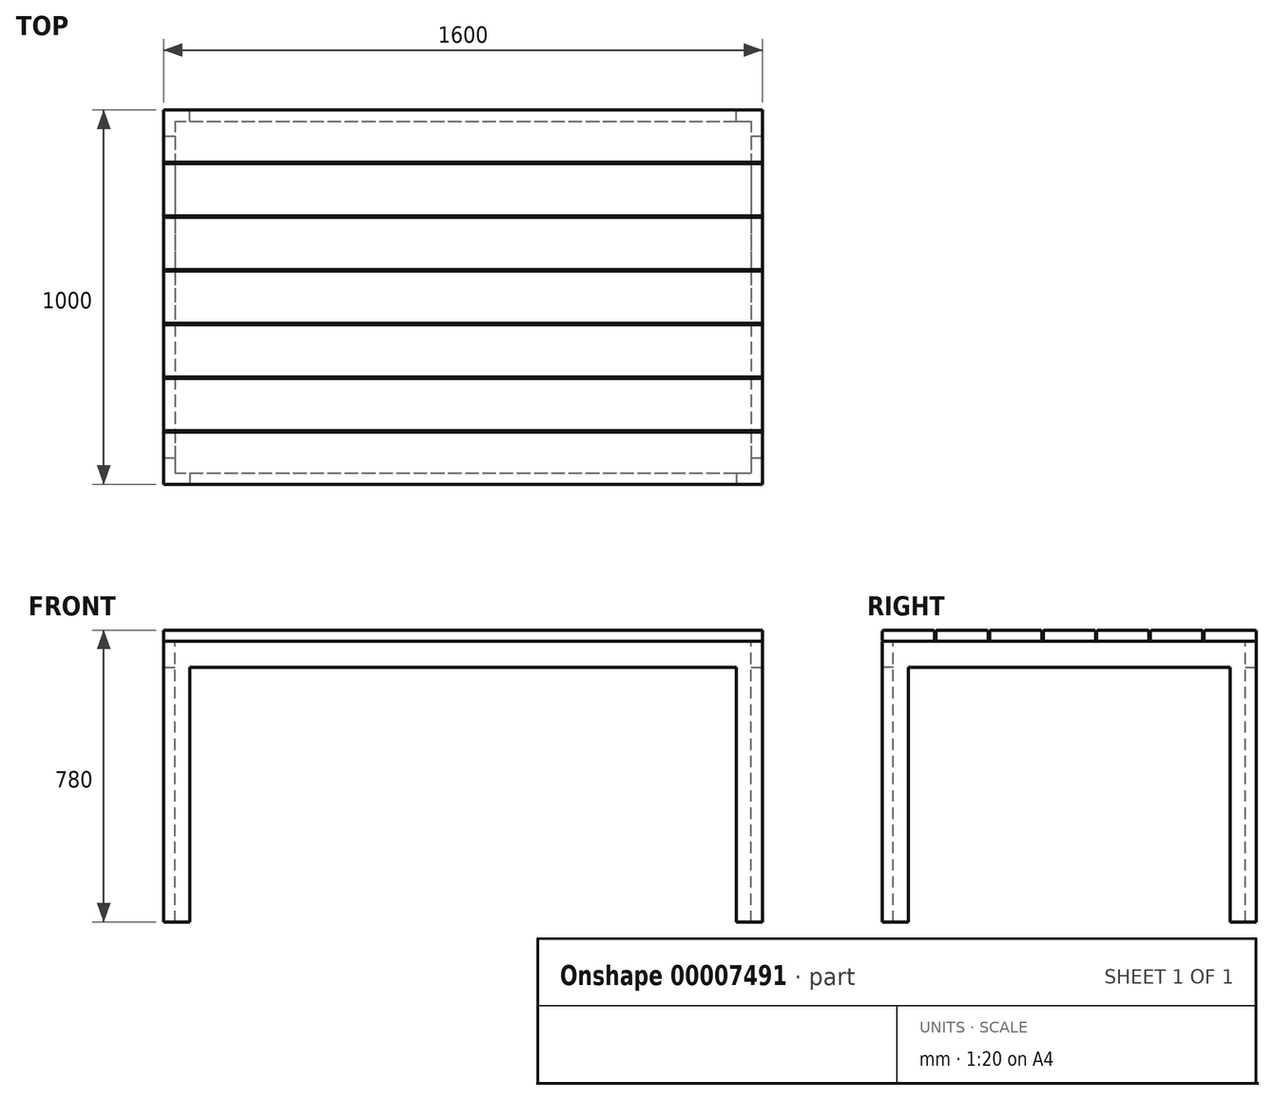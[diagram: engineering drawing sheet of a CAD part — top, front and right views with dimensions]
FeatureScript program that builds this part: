
annotation { "Feature Type Name" : "Feature", "Feature Type Description" : "" }
export const myFeature = defineFeature(function(context is Context, id is Id, definition is map)
    precondition{}
    {
        {
            var Q0;
            Q0=qCreatedBy(makeId("Top.planeOp"),FACE);
            var sketch = newSketch(context, id + "F0", { "sketchPlane" : qUnion([Q0])});
            skLineSegment(sketch, "E0.rect.bottom", {"start": v(-800, 500) * mm, "end": v(800, 500) * mm});
            skLineSegment(sketch, "E0.rect.top", {"start": v(-800, -500) * mm, "end": v(800, -500) * mm});
            skLineSegment(sketch, "E0.rect.left", {"start": v(-800, 500) * mm, "end": v(-800, -500) * mm});
            skLineSegment(sketch, "E0.rect.right", {"start": v(800, 500) * mm, "end": v(800, -500) * mm});
            skPoint(sketch, "E0.rect.middle", {"position": v(0, 0) * mm});
            skLineSegment(sketch, "E1.rect.bottom", {"start": v(-770, 470) * mm, "end": v(770, 470) * mm});
            skLineSegment(sketch, "E1.rect.top", {"start": v(-770, -470) * mm, "end": v(770, -470) * mm});
            skLineSegment(sketch, "E1.rect.left", {"start": v(-770, 470) * mm, "end": v(-770, -470) * mm});
            skLineSegment(sketch, "E1.rect.right", {"start": v(770, 470) * mm, "end": v(770, -470) * mm});
            skLineSegment(sketch, "E2", {"start": v(-800, -430) * mm, "end": v(-770, -430) * mm});
            skLineSegment(sketch, "E3", {"start": v(-730, -470) * mm, "end": v(-730, -500) * mm});
            skLineSegment(sketch, "E4", {"start": v(-800, 430) * mm, "end": v(-770, 430) * mm});
            skLineSegment(sketch, "E5", {"start": v(-730, 470) * mm, "end": v(-730, 500) * mm});
            skLineSegment(sketch, "E6", {"start": v(730, 470) * mm, "end": v(730, 500) * mm});
            skLineSegment(sketch, "E7", {"start": v(770, 430) * mm, "end": v(800, 430) * mm});
            skLineSegment(sketch, "E8", {"start": v(770, -430) * mm, "end": v(800, -430) * mm});
            skLineSegment(sketch, "E9", {"start": v(730, -470) * mm, "end": v(730, -500) * mm});
            skSolve(sketch);
        }
        {
            var Q0;
            {var subQ1=sQuery(id+"F0.wireOp",EDGE,"E2");Q0=makeQuery(id+"F0.imprint","IMPRINT",FACE,{"disambiguationData":[TD([[makeQuery(id+"F0.imprint","IMPRINT",EDGE,{"derivedFrom":subQ1}),-1.0]])]});}
            var Q1;
            {var subQ0=sQuery(id+"F0.wireOp",EDGE,"E4");Q1=makeQuery(id+"F0.imprint","IMPRINT",FACE,{"disambiguationData":[TD([[makeQuery(id+"F0.imprint","IMPRINT",EDGE,{"derivedFrom":subQ0}),1.0]])]});}
            var Q2;
            {var subQ1=sQuery(id+"F0.wireOp",EDGE,"E6");Q2=makeQuery(id+"F0.imprint","IMPRINT",FACE,{"disambiguationData":[TD([[makeQuery(id+"F0.imprint","IMPRINT",EDGE,{"derivedFrom":subQ1}),-1.0]])]});}
            var Q3;
            {var subQ1=sQuery(id+"F0.wireOp",EDGE,"E8");Q3=makeQuery(id+"F0.imprint","IMPRINT",FACE,{"disambiguationData":[TD([[makeQuery(id+"F0.imprint","IMPRINT",EDGE,{"derivedFrom":subQ1}),-1.0]])]});}
            extrude(context, id + "F1", {"entities" : qUnion([Q0, Q1, Q2, Q3]), "oppositeDirection" : true, "depth" : 750 * mm});
        }
        {
            var Q0;
            {var subQ1=sQuery(id+"F0.wireOp",EDGE,"E2");Q0=makeQuery(id+"F0.imprint","IMPRINT",FACE,{"disambiguationData":[TD([[makeQuery(id+"F0.imprint","IMPRINT",EDGE,{"derivedFrom":subQ1}),1.0]])]});}
            var Q1;
            {var subQ1=sQuery(id+"F0.wireOp",EDGE,"E5");Q1=makeQuery(id+"F0.imprint","IMPRINT",FACE,{"disambiguationData":[TD([[makeQuery(id+"F0.imprint","IMPRINT",EDGE,{"derivedFrom":subQ1}),-1.0]])]});}
            var Q2;
            {var subQ1=sQuery(id+"F0.wireOp",EDGE,"E3");Q2=makeQuery(id+"F0.imprint","IMPRINT",FACE,{"disambiguationData":[TD([[makeQuery(id+"F0.imprint","IMPRINT",EDGE,{"derivedFrom":subQ1}),1.0]])]});}
            var Q3;
            {var subQ1=sQuery(id+"F0.wireOp",EDGE,"E7");Q3=makeQuery(id+"F0.imprint","IMPRINT",FACE,{"disambiguationData":[TD([[makeQuery(id+"F0.imprint","IMPRINT",EDGE,{"derivedFrom":subQ1}),-1.0]])]});}
            extrude(context, id + "F2", {"entities" : qUnion([Q0, Q1, Q2, Q3]), "operationType" : NewBodyOperationType.ADD, "oppositeDirection" : true, "depth" : 70 * mm});
        }
        {
            var Q0;
            Q0=qCreatedBy(makeId("Top.planeOp"),FACE);
            var sketch = newSketch(context, id + "F3", { "sketchPlane" : qUnion([Q0])});
            skLineSegment(sketch, "E10.bottom", {"start": v(-800, -500) * mm, "end": v(800, -500) * mm});
            skLineSegment(sketch, "E10.top", {"start": v(-800, -360.3) * mm, "end": v(800, -360.3) * mm});
            skLineSegment(sketch, "E10.left", {"start": v(-800, -500) * mm, "end": v(-800, -360.3) * mm});
            skLineSegment(sketch, "E10.right", {"start": v(800, -500) * mm, "end": v(800, -360.3) * mm});
            skLineSegment(sketch, "E11.0.1.0", {"start": v(-800, -356.62) * mm, "end": v(-800, -216.92) * mm});
            skLineSegment(sketch, "E11.0.1.1", {"start": v(-800, -356.62) * mm, "end": v(800, -356.62) * mm});
            skLineSegment(sketch, "E11.0.1.2", {"start": v(-800, -216.92) * mm, "end": v(800, -216.92) * mm});
            skLineSegment(sketch, "E11.0.1.3", {"start": v(800, -356.62) * mm, "end": v(800, -216.92) * mm});
            skLineSegment(sketch, "E11.0.2.0", {"start": v(-800, -213.23) * mm, "end": v(-800, -73.53) * mm});
            skLineSegment(sketch, "E11.0.2.1", {"start": v(-800, -213.23) * mm, "end": v(800, -213.23) * mm});
            skLineSegment(sketch, "E11.0.2.2", {"start": v(-800, -73.53) * mm, "end": v(800, -73.53) * mm});
            skLineSegment(sketch, "E11.0.2.3", {"start": v(800, -213.23) * mm, "end": v(800, -73.53) * mm});
            skLineSegment(sketch, "E11.0.3.0", {"start": v(-800, -69.85) * mm, "end": v(-800, 69.85) * mm});
            skLineSegment(sketch, "E11.0.3.1", {"start": v(-800, -69.85) * mm, "end": v(800, -69.85) * mm});
            skLineSegment(sketch, "E11.0.3.2", {"start": v(-800, 69.85) * mm, "end": v(800, 69.85) * mm});
            skLineSegment(sketch, "E11.0.3.3", {"start": v(800, -69.85) * mm, "end": v(800, 69.85) * mm});
            skLineSegment(sketch, "E11.0.4.0", {"start": v(-800, 73.53) * mm, "end": v(-800, 213.23) * mm});
            skLineSegment(sketch, "E11.0.4.1", {"start": v(-800, 73.53) * mm, "end": v(800, 73.53) * mm});
            skLineSegment(sketch, "E11.0.4.2", {"start": v(-800, 213.23) * mm, "end": v(800, 213.23) * mm});
            skLineSegment(sketch, "E11.0.4.3", {"start": v(800, 73.53) * mm, "end": v(800, 213.23) * mm});
            skLineSegment(sketch, "E11.0.5.0", {"start": v(-800, 216.92) * mm, "end": v(-800, 356.62) * mm});
            skLineSegment(sketch, "E11.0.5.1", {"start": v(-800, 216.92) * mm, "end": v(800, 216.92) * mm});
            skLineSegment(sketch, "E11.0.5.2", {"start": v(-800, 356.62) * mm, "end": v(800, 356.62) * mm});
            skLineSegment(sketch, "E11.0.5.3", {"start": v(800, 216.92) * mm, "end": v(800, 356.62) * mm});
            skLineSegment(sketch, "E11.0.6.0", {"start": v(-800, 360.3) * mm, "end": v(-800, 500) * mm});
            skLineSegment(sketch, "E11.0.6.1", {"start": v(-800, 360.3) * mm, "end": v(800, 360.3) * mm});
            skLineSegment(sketch, "E11.0.6.2", {"start": v(-800, 500) * mm, "end": v(800, 500) * mm});
            skLineSegment(sketch, "E11.0.6.3", {"start": v(800, 360.3) * mm, "end": v(800, 500) * mm});
            skLineSegment(sketch, "E11.direction1", {"start": v(-800, -500) * mm, "end": v(-774.6, -500) * mm, "construction": true});
            skLineSegment(sketch, "E11.direction2", {"start": v(-800, -500) * mm, "end": v(-800, -356.62) * mm, "construction": true});
            skSolve(sketch);
        }
        {
            var Q0;
            Q0=makeQuery(id+"F3.imprint","IMPRINT",FACE,{"disambiguationData":[TD([[makeQuery(id+"F3.imprint","IMPRINT",EDGE,{"derivedFrom":sQuery(id+"F3.wireOp",EDGE,"E10.bottom")}),1.0]])]});
            var Q1;
            Q1=makeQuery(id+"F3.imprint","IMPRINT",FACE,{"disambiguationData":[TD([[makeQuery(id+"F3.imprint","IMPRINT",EDGE,{"derivedFrom":sQuery(id+"F3.wireOp",EDGE,"E11.0.1.0")}),-1.0]])]});
            var Q2;
            Q2=makeQuery(id+"F3.imprint","IMPRINT",FACE,{"disambiguationData":[TD([[makeQuery(id+"F3.imprint","IMPRINT",EDGE,{"derivedFrom":sQuery(id+"F3.wireOp",EDGE,"E11.0.2.0")}),-1.0]])]});
            var Q3;
            Q3=makeQuery(id+"F3.imprint","IMPRINT",FACE,{"disambiguationData":[TD([[makeQuery(id+"F3.imprint","IMPRINT",EDGE,{"derivedFrom":sQuery(id+"F3.wireOp",EDGE,"E11.0.3.0")}),-1.0]])]});
            var Q4;
            Q4=makeQuery(id+"F3.imprint","IMPRINT",FACE,{"disambiguationData":[TD([[makeQuery(id+"F3.imprint","IMPRINT",EDGE,{"derivedFrom":sQuery(id+"F3.wireOp",EDGE,"E11.0.4.0")}),-1.0]])]});
            var Q5;
            Q5=makeQuery(id+"F3.imprint","IMPRINT",FACE,{"disambiguationData":[TD([[makeQuery(id+"F3.imprint","IMPRINT",EDGE,{"derivedFrom":sQuery(id+"F3.wireOp",EDGE,"E11.0.5.0")}),-1.0]])]});
            var Q6;
            Q6=makeQuery(id+"F3.imprint","IMPRINT",FACE,{"disambiguationData":[TD([[makeQuery(id+"F3.imprint","IMPRINT",EDGE,{"derivedFrom":sQuery(id+"F3.wireOp",EDGE,"E11.0.6.0")}),-1.0]])]});
            var Q7;
            Q7=makeQuery(id+"F3.imprint","IMPRINT",FACE,{"disambiguationData":[TD([[makeQuery(id+"F3.imprint","IMPRINT",EDGE,{"derivedFrom":sQuery(id+"F3.wireOp",EDGE,"E11.0.7.0")}),-1.0]])]});
            var Q8;
            Q8=makeQuery(id+"F3.imprint","IMPRINT",FACE,{"disambiguationData":[TD([[makeQuery(id+"F3.imprint","IMPRINT",EDGE,{"derivedFrom":sQuery(id+"F3.wireOp",EDGE,"E11.0.8.0")}),-1.0]])]});
            var Q9;
            Q9=makeQuery(id+"F3.imprint","IMPRINT",FACE,{"disambiguationData":[TD([[makeQuery(id+"F3.imprint","IMPRINT",EDGE,{"derivedFrom":sQuery(id+"F3.wireOp",EDGE,"E11.0.9.0")}),-1.0]])]});
            var Q10;
            Q10=makeQuery(id+"F3.imprint","IMPRINT",FACE,{"disambiguationData":[TD([[makeQuery(id+"F3.imprint","IMPRINT",EDGE,{"derivedFrom":sQuery(id+"F3.wireOp",EDGE,"E11.0.10.0")}),-1.0]])]});
            extrude(context, id + "F4", {"entities" : qUnion([Q0, Q1, Q2, Q3, Q4, Q5, Q6, Q7, Q8, Q9, Q10]), "depth" : 30 * mm});
        }
        {
            var Q0;
            Q0=makeQuery(id+"F4.opExtrude","CAP_EDGE",EDGE,{"disambiguationData":[OSD([sQuery(id+"F3.wireOp",EDGE,"E11.0.8.1")])],"isStart":false});
            var Q1;
            Q1=makeQuery(id+"F4.opExtrude","CAP_EDGE",EDGE,{"disambiguationData":[OSD([sQuery(id+"F3.wireOp",EDGE,"E11.0.10.1")])],"isStart":false});
            var Q2;
            Q2=makeQuery(id+"F4.opExtrude","CAP_EDGE",EDGE,{"disambiguationData":[OSD([sQuery(id+"F3.wireOp",EDGE,"E10.bottom")])],"isStart":false});
            var Q3;
            Q3=makeQuery(id+"F4.opExtrude","CAP_EDGE",EDGE,{"disambiguationData":[OSD([sQuery(id+"F3.wireOp",EDGE,"E11.0.2.1")])],"isStart":false});
            var Q4;
            Q4=makeQuery(id+"F4.opExtrude","CAP_EDGE",EDGE,{"disambiguationData":[OSD([sQuery(id+"F3.wireOp",EDGE,"E10.top")])],"isStart":false});
            var Q5;
            Q5=makeQuery(id+"F4.opExtrude","CAP_EDGE",EDGE,{"disambiguationData":[OSD([sQuery(id+"F3.wireOp",EDGE,"E11.0.6.1")])],"isStart":false});
            var Q6;
            Q6=makeQuery(id+"F4.opExtrude","CAP_EDGE",EDGE,{"disambiguationData":[OSD([sQuery(id+"F3.wireOp",EDGE,"E11.0.4.1")])],"isStart":false});
            var Q7;
            Q7=makeQuery(id+"F4.opExtrude","CAP_EDGE",EDGE,{"disambiguationData":[OSD([sQuery(id+"F3.wireOp",EDGE,"E11.0.2.2")])],"isStart":false});
            var Q8;
            Q8=makeQuery(id+"F4.opExtrude","CAP_EDGE",EDGE,{"disambiguationData":[OSD([sQuery(id+"F3.wireOp",EDGE,"E11.0.10.2")])],"isStart":false});
            var Q9;
            Q9=makeQuery(id+"F4.opExtrude","CAP_EDGE",EDGE,{"disambiguationData":[OSD([sQuery(id+"F3.wireOp",EDGE,"E11.0.8.2")])],"isStart":false});
            var Q10;
            Q10=makeQuery(id+"F4.opExtrude","CAP_EDGE",EDGE,{"disambiguationData":[OSD([sQuery(id+"F3.wireOp",EDGE,"E11.0.6.2")])],"isStart":false});
            var Q11;
            Q11=makeQuery(id+"F4.opExtrude","CAP_EDGE",EDGE,{"disambiguationData":[OSD([sQuery(id+"F3.wireOp",EDGE,"E11.0.4.2")])],"isStart":false});
            var Q12;
            Q12=makeQuery(id+"F4.opExtrude","CAP_EDGE",EDGE,{"disambiguationData":[OSD([sQuery(id+"F3.wireOp",EDGE,"E11.0.9.1")])],"isStart":false});
            var Q13;
            Q13=makeQuery(id+"F4.opExtrude","CAP_EDGE",EDGE,{"disambiguationData":[OSD([sQuery(id+"F3.wireOp",EDGE,"E11.0.7.1")])],"isStart":false});
            var Q14;
            Q14=makeQuery(id+"F4.opExtrude","CAP_EDGE",EDGE,{"disambiguationData":[OSD([sQuery(id+"F3.wireOp",EDGE,"E11.0.5.1")])],"isStart":false});
            var Q15;
            Q15=makeQuery(id+"F4.opExtrude","CAP_EDGE",EDGE,{"disambiguationData":[OSD([sQuery(id+"F3.wireOp",EDGE,"E11.0.3.1")])],"isStart":false});
            var Q16;
            Q16=makeQuery(id+"F4.opExtrude","CAP_EDGE",EDGE,{"disambiguationData":[OSD([sQuery(id+"F3.wireOp",EDGE,"E11.0.3.2")])],"isStart":false});
            var Q17;
            Q17=makeQuery(id+"F4.opExtrude","CAP_EDGE",EDGE,{"disambiguationData":[OSD([sQuery(id+"F3.wireOp",EDGE,"E11.0.1.2")])],"isStart":false});
            var Q18;
            Q18=makeQuery(id+"F4.opExtrude","CAP_EDGE",EDGE,{"disambiguationData":[OSD([sQuery(id+"F3.wireOp",EDGE,"E11.0.7.2")])],"isStart":false});
            var Q19;
            Q19=makeQuery(id+"F4.opExtrude","CAP_EDGE",EDGE,{"disambiguationData":[OSD([sQuery(id+"F3.wireOp",EDGE,"E11.0.9.2")])],"isStart":false});
            var Q20;
            Q20=makeQuery(id+"F4.opExtrude","CAP_EDGE",EDGE,{"disambiguationData":[OSD([sQuery(id+"F3.wireOp",EDGE,"E11.0.5.2")])],"isStart":false});
            var Q21;
            Q21=makeQuery(id+"F4.opExtrude","CAP_EDGE",EDGE,{"disambiguationData":[OSD([sQuery(id+"F3.wireOp",EDGE,"E11.0.1.1")])],"isStart":false});
            var Q22;
            Q22=makeQuery(id+"F4.opExtrude","CAP_EDGE",EDGE,{"disambiguationData":[OSD([sQuery(id+"F3.wireOp",EDGE,"E10.bottom")])],"isStart":true});
            var Q23;
            Q23=makeQuery(id+"F4.opExtrude","CAP_EDGE",EDGE,{"disambiguationData":[OSD([sQuery(id+"F3.wireOp",EDGE,"E11.0.5.1")])],"isStart":true});
            var Q24;
            Q24=makeQuery(id+"F4.opExtrude","CAP_EDGE",EDGE,{"disambiguationData":[OSD([sQuery(id+"F3.wireOp",EDGE,"E11.0.2.2")])],"isStart":true});
            var Q25;
            Q25=makeQuery(id+"F4.opExtrude","CAP_EDGE",EDGE,{"disambiguationData":[OSD([sQuery(id+"F3.wireOp",EDGE,"E11.0.6.2")])],"isStart":true});
            var Q26;
            Q26=makeQuery(id+"F4.opExtrude","CAP_EDGE",EDGE,{"disambiguationData":[OSD([sQuery(id+"F3.wireOp",EDGE,"E11.0.4.2")])],"isStart":true});
            var Q27;
            Q27=makeQuery(id+"F4.opExtrude","CAP_EDGE",EDGE,{"disambiguationData":[OSD([sQuery(id+"F3.wireOp",EDGE,"E11.0.10.2")])],"isStart":true});
            var Q28;
            Q28=makeQuery(id+"F4.opExtrude","CAP_EDGE",EDGE,{"disambiguationData":[OSD([sQuery(id+"F3.wireOp",EDGE,"E11.0.8.2")])],"isStart":true});
            var Q29;
            Q29=makeQuery(id+"F4.opExtrude","CAP_EDGE",EDGE,{"disambiguationData":[OSD([sQuery(id+"F3.wireOp",EDGE,"E11.0.8.1")])],"isStart":true});
            var Q30;
            Q30=makeQuery(id+"F4.opExtrude","CAP_EDGE",EDGE,{"disambiguationData":[OSD([sQuery(id+"F3.wireOp",EDGE,"E11.0.10.1")])],"isStart":true});
            var Q31;
            Q31=makeQuery(id+"F4.opExtrude","CAP_EDGE",EDGE,{"disambiguationData":[OSD([sQuery(id+"F3.wireOp",EDGE,"E11.0.6.1")])],"isStart":true});
            var Q32;
            Q32=makeQuery(id+"F4.opExtrude","CAP_EDGE",EDGE,{"disambiguationData":[OSD([sQuery(id+"F3.wireOp",EDGE,"E11.0.4.1")])],"isStart":true});
            var Q33;
            Q33=makeQuery(id+"F4.opExtrude","CAP_EDGE",EDGE,{"disambiguationData":[OSD([sQuery(id+"F3.wireOp",EDGE,"E11.0.2.1")])],"isStart":true});
            var Q34;
            Q34=makeQuery(id+"F4.opExtrude","CAP_EDGE",EDGE,{"disambiguationData":[OSD([sQuery(id+"F3.wireOp",EDGE,"E10.top")])],"isStart":true});
            var Q35;
            Q35=makeQuery(id+"F4.opExtrude","CAP_EDGE",EDGE,{"disambiguationData":[OSD([sQuery(id+"F3.wireOp",EDGE,"E11.0.7.1")])],"isStart":true});
            var Q36;
            Q36=makeQuery(id+"F4.opExtrude","CAP_EDGE",EDGE,{"disambiguationData":[OSD([sQuery(id+"F3.wireOp",EDGE,"E11.0.9.2")])],"isStart":true});
            var Q37;
            Q37=makeQuery(id+"F4.opExtrude","CAP_EDGE",EDGE,{"disambiguationData":[OSD([sQuery(id+"F3.wireOp",EDGE,"E11.0.7.2")])],"isStart":true});
            var Q38;
            Q38=makeQuery(id+"F4.opExtrude","CAP_EDGE",EDGE,{"disambiguationData":[OSD([sQuery(id+"F3.wireOp",EDGE,"E11.0.5.2")])],"isStart":true});
            var Q39;
            Q39=makeQuery(id+"F4.opExtrude","CAP_EDGE",EDGE,{"disambiguationData":[OSD([sQuery(id+"F3.wireOp",EDGE,"E11.0.3.1")])],"isStart":true});
            var Q40;
            Q40=makeQuery(id+"F4.opExtrude","CAP_EDGE",EDGE,{"disambiguationData":[OSD([sQuery(id+"F3.wireOp",EDGE,"E11.0.1.1")])],"isStart":true});
            var Q41;
            Q41=makeQuery(id+"F4.opExtrude","CAP_EDGE",EDGE,{"disambiguationData":[OSD([sQuery(id+"F3.wireOp",EDGE,"E11.0.9.1")])],"isStart":true});
            var Q42;
            Q42=makeQuery(id+"F4.opExtrude","CAP_EDGE",EDGE,{"disambiguationData":[OSD([sQuery(id+"F3.wireOp",EDGE,"E11.0.1.2")])],"isStart":true});
            var Q43;
            Q43=makeQuery(id+"F4.opExtrude","CAP_EDGE",EDGE,{"disambiguationData":[OSD([sQuery(id+"F3.wireOp",EDGE,"E11.0.3.2")])],"isStart":true});
            fillet(context, id + "F5", {"entities" : qUnion([Q0, Q1, Q2, Q3, Q4, Q5, Q6, Q7, Q8, Q9, Q10, Q11, Q12, Q13, Q14, Q15, Q16, Q17, Q18, Q19, Q20, Q21, Q22, Q23, Q24, Q25, Q26, Q27, Q28, Q29, Q30, Q31, Q32, Q33, Q34, Q35, Q36, Q37, Q38, Q39, Q40, Q41, Q42, Q43]), "radius" : 5.08 * mm, "tangentPropagation" : true, "allowEdgeOverflow" : false});
        }
    });
